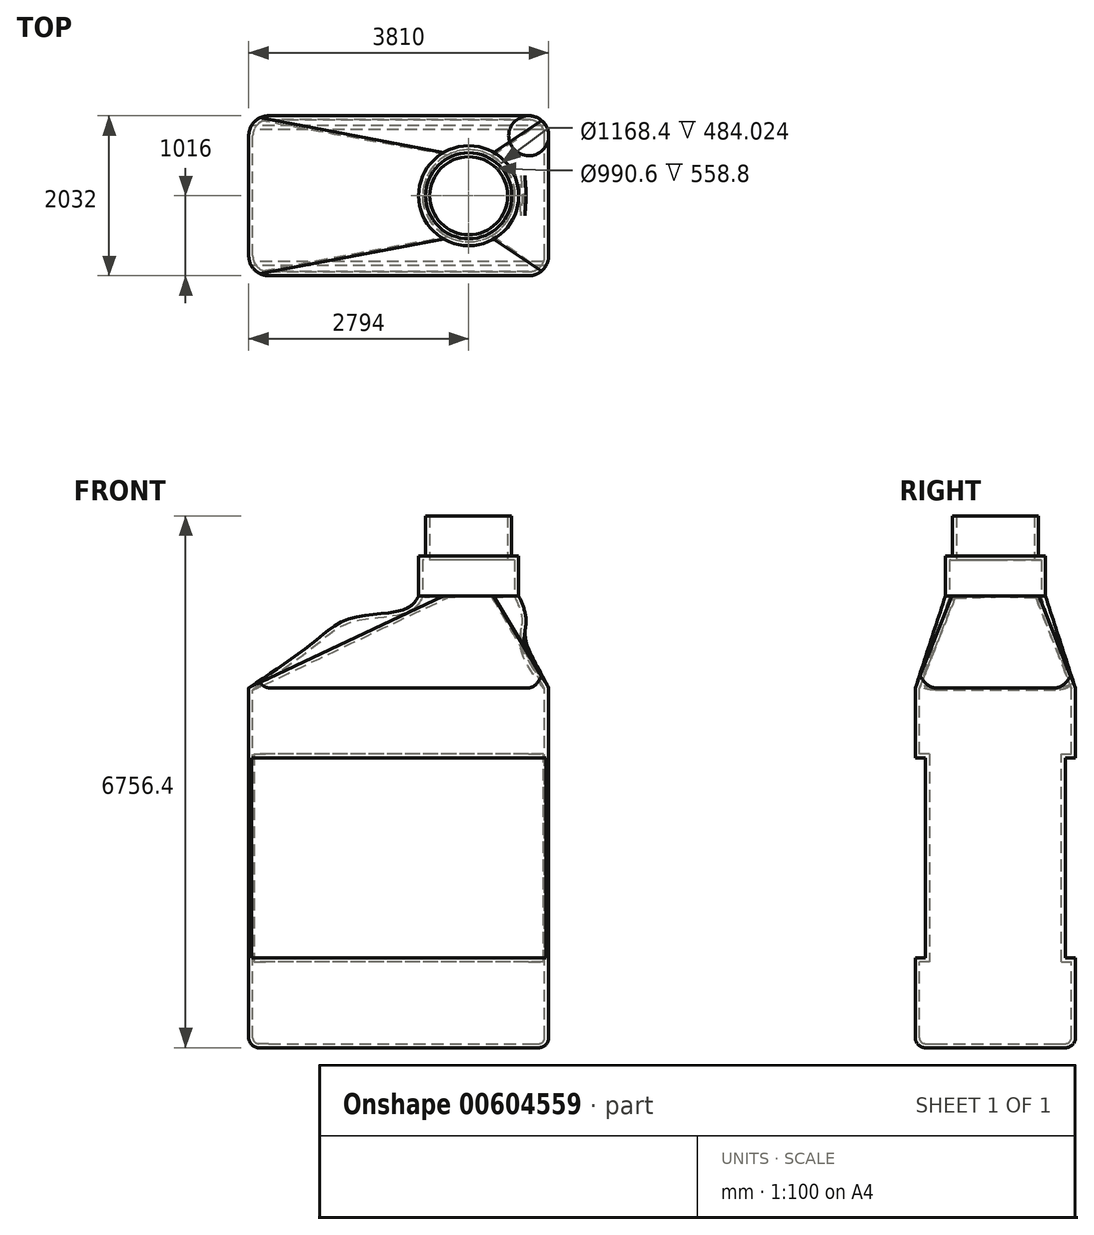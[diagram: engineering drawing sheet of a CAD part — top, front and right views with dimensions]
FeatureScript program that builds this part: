
annotation { "Feature Type Name" : "Feature", "Feature Type Description" : "" }
export const myFeature = defineFeature(function(context is Context, id is Id, definition is map)
    precondition{}
    {
        {
            var Q0;
            Q0=qCreatedBy(makeId("Top.planeOp"),FACE);
            var sketch = newSketch(context, id + "F0", { "sketchPlane" : qUnion([Q0])});
            skLineSegment(sketch, "E0.bottom", {"start": v(0, 0) * mm, "end": v(3810, 0) * mm});
            skLineSegment(sketch, "E0.top", {"start": v(0, 2032) * mm, "end": v(3810, 2032) * mm});
            skLineSegment(sketch, "E0.left", {"start": v(0, 0) * mm, "end": v(0, 2032) * mm});
            skLineSegment(sketch, "E0.right", {"start": v(3810, 0) * mm, "end": v(3810, 2032) * mm});
            skSolve(sketch);
        }
        {
            var Q0;
            Q0 = qSketchRegion(id + "F0", true);
            var Q1;
            Q1=makeQuery(id+"F0.imprint","IMPRINT",FACE,{"disambiguationData":[TD([[makeQuery(id+"F0.imprint","IMPRINT",EDGE,{"derivedFrom":sQuery(id+"F0.wireOp",EDGE,"E0.bottom")}),1.0]])]});
            extrude(context, id + "F1", {"entities" : qUnion([Q0, Q1]), "endBound" : BoundingType.SYMMETRIC, "depth" : 4572 * mm, "offsetDistance" : 25.4 * mm});
        }
        {
            var Q0;
            Q0=makeQuery(id+"F1.opExtrude","CAP_FACE",FACE,{"disambiguationData":[OSD([sQuery(id+"F0.wireOp",EDGE,"E0.bottom"),sQuery(id+"F0.wireOp",EDGE,"E0.top"),sQuery(id+"F0.wireOp",EDGE,"E0.left"),sQuery(id+"F0.wireOp",EDGE,"E0.right")])],"isStart":false});
            cPlane(context, id + "F2", {"entities" : qUnion([Q0]), "cplaneType" : CPlaneType.OFFSET, "offset" : 1168.4 * mm, "width" : 152.4 * mm, "height" : 152.4 * mm});
        }
        {
            var Q0;
            Q0=qCreatedBy(id+"F2.planeOp",FACE);
            var sketch = newSketch(context, id + "F3", { "sketchPlane" : qUnion([Q0])});
            skCircle(sketch, "E1", {"center": v(2794, 1016) * mm, "radius": 635 * mm});
            skSolve(sketch);
        }
        {
            var Q0;
            Q0=makeQuery(id+"F3.imprint","IMPRINT",FACE,{"disambiguationData":[TD([[makeQuery(id+"F3.imprint","IMPRINT",EDGE,{"derivedFrom":sQuery(id+"F3.wireOp",EDGE,"E1")}),1.0]])]});
            var Q1;
            Q1=sQuery(id+"F3.wireOp",EDGE,"E1");
            extrude(context, id + "F4", {"entities" : qUnion([Q0]), "surfaceEntities" : qUnion([Q1]), "depth" : 508 * mm, "offsetDistance" : 25.4 * mm});
        }
        {
            var Q0;
            Q0=makeQuery(id+"F4.opExtrude","CAP_FACE",FACE,{"disambiguationData":[OSD([sQuery(id+"F3.wireOp",EDGE,"E1")])],"isStart":false});
            var sketch = newSketch(context, id + "F5", { "sketchPlane" : qUnion([Q0])});
            skCircle(sketch, "E2", {"center": v(2794, 1016) * mm, "radius": 546.1 * mm});
            skSolve(sketch);
        }
        {
            var Q0;
            Q0=makeQuery(id+"F5.imprint","IMPRINT",FACE,{"disambiguationData":[TD([[makeQuery(id+"F5.imprint","IMPRINT",EDGE,{"derivedFrom":sQuery(id+"F5.wireOp",EDGE,"E2")}),1.0]])]});
            extrude(context, id + "F6", {"entities" : qUnion([Q0]), "operationType" : NewBodyOperationType.ADD, "depth" : 508 * mm, "offsetDistance" : 25.4 * mm});
        }
        {
            var Q0;
            Q0=makeQuery(id+"F1.opExtrude","SWEPT_FACE",FACE,{"disambiguationData":[OSD([sQuery(id+"F0.wireOp",EDGE,"E0.bottom")])]});
            var Q1;
            Q1=makeQuery(id+"F1.opExtrude","SWEPT_FACE",FACE,{"disambiguationData":[OSD([sQuery(id+"F0.wireOp",EDGE,"E0.top")])]});
            cPlane(context, id + "F7", {"entities" : qUnion([Q0, Q1]), "cplaneType" : CPlaneType.MID_PLANE, "offset" : 25.4 * mm, "width" : 152.4 * mm, "height" : 152.4 * mm});
        }
        {
            var Q0;
            Q0=qCreatedBy(id+"F7.planeOp",FACE);
            var sketch = newSketch(context, id + "F8", { "sketchPlane" : qUnion([Q0])});
            skLineSegment(sketch, "E3.0", {"start": v(0, 2286) * mm, "end": v(3810, 2286) * mm, "construction": true});
            skLineSegment(sketch, "E4.1", {"start": v(2159, 3454.4) * mm, "end": v(3429, 3454.4) * mm, "construction": true});
            skFitSpline(sketch, "E5", {"points": [v(3810, 2286) * mm, v(3502.07, 2804.73) * mm, v(3521.76, 3148.6) * mm, v(3429, 3454.4) * mm], "startDerivative": vector(-1043.9, 1329.22) * mm, "endDerivative": vector(-461.76, 1029.77) * mm});
            skFitSpline(sketch, "E6", {"points": [v(0, 2286) * mm, v(826.85, 2867.04) * mm, v(1279.75, 3162.6) * mm, v(1997.53, 3289.6) * mm, v(2159, 3454.4) * mm], "startDerivative": vector(2814.6, 1867.49) * mm, "endDerivative": vector(680.46, 1210.27) * mm});
            skSolve(sketch);
        }
        {
            var Q1;
            Q1=makeQuery(id+"F1.opExtrude","CAP_FACE",FACE,{"disambiguationData":[OSD([sQuery(id+"F0.wireOp",EDGE,"E0.bottom"),sQuery(id+"F0.wireOp",EDGE,"E0.top"),sQuery(id+"F0.wireOp",EDGE,"E0.left"),sQuery(id+"F0.wireOp",EDGE,"E0.right")])],"isStart":false});
            var Q2;
            Q2=makeQuery(id+"F4.opExtrude","CAP_FACE",FACE,{"disambiguationData":[OSD([sQuery(id+"F3.wireOp",EDGE,"E1")])],"isStart":true});
            var Q3;
            Q3=sQuery(id+"F8.wireOp",EDGE,"E6");
            var Q4;
            Q4=sQuery(id+"F8.wireOp",EDGE,"E5");
            loft(context, id + "F9", {"operationType" : NewBodyOperationType.ADD, "addGuides" : true, "sheetProfilesArray" : [{ "sheetProfileEntities" : qUnion([Q1]) }, { "sheetProfileEntities" : qUnion([Q2]) }], "guidesArray" : [{ "guideEntities" : qUnion([Q3]), "guideDerivativeType" : LoftGuideDerivativeType.DEFAULT, "guideDerivativeMagnitude" : 1 }, { "guideEntities" : qUnion([Q4]), "guideDerivativeType" : LoftGuideDerivativeType.DEFAULT, "guideDerivativeMagnitude" : 1 }]});
        }
        {
            var Q0;
            Q0=makeQuery(id+"F1.opExtrude","SWEPT_FACE",FACE,{"disambiguationData":[OSD([sQuery(id+"F0.wireOp",EDGE,"E0.top")])]});
            var sketch = newSketch(context, id + "F10", { "sketchPlane" : qUnion([Q0])});
            skLineSegment(sketch, "E7.bottom", {"start": v(-3810, 1397) * mm, "end": v(0, 1397) * mm});
            skLineSegment(sketch, "E7.top", {"start": v(-3810, -1143) * mm, "end": v(0, -1143) * mm});
            skLineSegment(sketch, "E7.left", {"start": v(-3810, 1397) * mm, "end": v(-3810, -1143) * mm});
            skLineSegment(sketch, "E7.right", {"start": v(0, 1397) * mm, "end": v(0, -1143) * mm});
            skSolve(sketch);
        }
        {
            var Q0;
            Q0=makeQuery(id+"F10.imprint","IMPRINT",FACE,{"disambiguationData":[TD([[makeQuery(id+"F10.imprint","IMPRINT",EDGE,{"derivedFrom":sQuery(id+"F10.wireOp",EDGE,"E7.bottom")}),-1.0]])]});
            extrude(context, id + "F11", {"entities" : qUnion([Q0]), "operationType" : NewBodyOperationType.REMOVE, "oppositeDirection" : true, "depth" : 127 * mm, "offsetDistance" : 25.4 * mm});
        }
        {
            var Q0;
            Q0=makeQuery(id+"F1.opExtrude","SWEPT_FACE",FACE,{"disambiguationData":[OSD([sQuery(id+"F0.wireOp",EDGE,"E0.bottom")])]});
            var sketch = newSketch(context, id + "F12", { "sketchPlane" : qUnion([Q0])});
            skLineSegment(sketch, "E8.0", {"start": v(3810, 1397) * mm, "end": v(0, 1397) * mm});
            skLineSegment(sketch, "E9.0", {"start": v(3810, 1397) * mm, "end": v(3810, -1143) * mm});
            skLineSegment(sketch, "E10.0", {"start": v(3810, -1143) * mm, "end": v(0, -1143) * mm});
            skLineSegment(sketch, "E11.0", {"start": v(0, 1397) * mm, "end": v(0, -1143) * mm});
            skSolve(sketch);
        }
        {
            var Q0;
            Q0=makeQuery(id+"F12.imprint","IMPRINT",FACE,{"disambiguationData":[TD([[makeQuery(id+"F12.imprint","IMPRINT",EDGE,{"derivedFrom":sQuery(id+"F12.wireOp",EDGE,"E8.0")}),1.0]])]});
            extrude(context, id + "F13", {"entities" : qUnion([Q0]), "operationType" : NewBodyOperationType.REMOVE, "oppositeDirection" : true, "depth" : 127 * mm, "offsetDistance" : 25.4 * mm});
        }
        {
            var Q0;
            {var subQ3=sQuery(id+"F0.wireOp",EDGE,"E0.left");var subQ4=sQuery(id+"F0.wireOp",EDGE,"E0.bottom");Q0=makeQuery(id+"F13.boolean.opBoolean","SPLIT",EDGE,{"disambiguationData":[TD([makeQuery(id+"F13.opExtrude","SWEPT_FACE",FACE,{"disambiguationData":[OSD([sQuery(id+"F12.wireOp",EDGE,"E8.0")])]})])],"derivedFrom":makeQuery(id+"F1.opExtrude","SWEPT_EDGE",EDGE,{"disambiguationData":[OSD([subQ4,subQ3])]})});}
            var Q1;
            {var subQ0=sQuery(id+"F0.wireOp",EDGE,"E0.bottom");var subQ1=sQuery(id+"F0.wireOp",EDGE,"E0.left");Q1=makeQuery(id+"F13.boolean.opBoolean","SPLIT",EDGE,{"disambiguationData":[TD([makeQuery(id+"F13.opExtrude","SWEPT_FACE",FACE,{"disambiguationData":[OSD([sQuery(id+"F12.wireOp",EDGE,"E10.0")])]})])],"derivedFrom":makeQuery(id+"F1.opExtrude","SWEPT_EDGE",EDGE,{"disambiguationData":[OSD([subQ0,subQ1])]})});}
            var Q2;
            {var subQ0=sQuery(id+"F0.wireOp",EDGE,"E0.left");var subQ1=sQuery(id+"F0.wireOp",EDGE,"E0.top");Q2=makeQuery(id+"F11.boolean.opBoolean","SPLIT",EDGE,{"disambiguationData":[TD([makeQuery(id+"F11.opExtrude","SWEPT_FACE",FACE,{"disambiguationData":[OSD([sQuery(id+"F10.wireOp",EDGE,"E7.top")])]})])],"derivedFrom":makeQuery(id+"F1.opExtrude","SWEPT_EDGE",EDGE,{"disambiguationData":[OSD([subQ1,subQ0])]})});}
            var Q3;
            {var subQ2=sQuery(id+"F0.wireOp",EDGE,"E0.left");var subQ3=sQuery(id+"F0.wireOp",EDGE,"E0.top");Q3=makeQuery(id+"F11.boolean.opBoolean","SPLIT",EDGE,{"disambiguationData":[TD([makeQuery(id+"F11.opExtrude","SWEPT_FACE",FACE,{"disambiguationData":[OSD([sQuery(id+"F10.wireOp",EDGE,"E7.bottom")])]})])],"derivedFrom":makeQuery(id+"F1.opExtrude","SWEPT_EDGE",EDGE,{"disambiguationData":[OSD([subQ3,subQ2])]})});}
            var Q4;
            {var subQ0=sQuery(id+"F0.wireOp",EDGE,"E0.bottom");var subQ1=sQuery(id+"F0.wireOp",EDGE,"E0.right");Q4=makeQuery(id+"F13.boolean.opBoolean","SPLIT",EDGE,{"disambiguationData":[TD([makeQuery(id+"F13.opExtrude","SWEPT_FACE",FACE,{"disambiguationData":[OSD([sQuery(id+"F12.wireOp",EDGE,"E10.0")])]})])],"derivedFrom":makeQuery(id+"F1.opExtrude","SWEPT_EDGE",EDGE,{"disambiguationData":[OSD([subQ0,subQ1])]})});}
            var Q5;
            {var subQ1=sQuery(id+"F0.wireOp",EDGE,"E0.right");var subQ3=sQuery(id+"F0.wireOp",EDGE,"E0.bottom");Q5=makeQuery(id+"F13.boolean.opBoolean","SPLIT",EDGE,{"disambiguationData":[TD([makeQuery(id+"F13.opExtrude","SWEPT_FACE",FACE,{"disambiguationData":[OSD([sQuery(id+"F12.wireOp",EDGE,"E8.0")])]})])],"derivedFrom":makeQuery(id+"F1.opExtrude","SWEPT_EDGE",EDGE,{"disambiguationData":[OSD([subQ3,subQ1])]})});}
            var Q6;
            {var subQ2=sQuery(id+"F0.wireOp",EDGE,"E0.right");var subQ4=sQuery(id+"F0.wireOp",EDGE,"E0.top");Q6=makeQuery(id+"F11.boolean.opBoolean","SPLIT",EDGE,{"disambiguationData":[TD([makeQuery(id+"F11.opExtrude","SWEPT_FACE",FACE,{"disambiguationData":[OSD([sQuery(id+"F10.wireOp",EDGE,"E7.bottom")])]})])],"derivedFrom":makeQuery(id+"F1.opExtrude","SWEPT_EDGE",EDGE,{"disambiguationData":[OSD([subQ4,subQ2])]})});}
            var Q7;
            {var subQ0=sQuery(id+"F0.wireOp",EDGE,"E0.right");var subQ1=sQuery(id+"F0.wireOp",EDGE,"E0.top");Q7=makeQuery(id+"F11.boolean.opBoolean","SPLIT",EDGE,{"disambiguationData":[TD([makeQuery(id+"F11.opExtrude","SWEPT_FACE",FACE,{"disambiguationData":[OSD([sQuery(id+"F10.wireOp",EDGE,"E7.top")])]})])],"derivedFrom":makeQuery(id+"F1.opExtrude","SWEPT_EDGE",EDGE,{"disambiguationData":[OSD([subQ1,subQ0])]})});}
            fillet(context, id + "F14", {"entities" : qUnion([Q0, Q1, Q2, Q3, Q4, Q5, Q6, Q7]), "radius" : 254 * mm, "tangentPropagation" : true, "allowEdgeOverflow" : false});
        }
        {
            var Q0;
            Q0=makeQuery(id+"F1.opExtrude","CAP_EDGE",EDGE,{"disambiguationData":[OSD([sQuery(id+"F0.wireOp",EDGE,"E0.bottom")])],"isStart":true});
            var Q1;
            {var subQ0=sQuery(id+"F0.wireOp",EDGE,"E0.right");var subQ1=sQuery(id+"F0.wireOp",EDGE,"E0.left");var subQ2=sQuery(id+"F0.wireOp",EDGE,"E0.top");var subQ3=sQuery(id+"F0.wireOp",EDGE,"E0.bottom");Q1=makeQuery(id+"F14.opFillet","BLEND_EDGE",EDGE,{"blendedFrom":[makeQuery(id+"F13.boolean.opBoolean","SPLIT",EDGE,{"disambiguationData":[TD([makeQuery(id+"F13.opExtrude","SWEPT_FACE",FACE,{"disambiguationData":[OSD([sQuery(id+"F12.wireOp",EDGE,"E8.0")])]})])],"derivedFrom":makeQuery(id+"F1.opExtrude","SWEPT_EDGE",EDGE,{"disambiguationData":[OSD([subQ3,subQ1])]})}),makeQuery(id+"F1.opExtrude","CAP_FACE",FACE,{"disambiguationData":[OSD([subQ3,subQ2,subQ1,subQ0])],"isStart":true})],"blendedInto":[makeQuery(id+"F1.opExtrude","CAP_FACE",FACE,{"disambiguationData":[OSD([subQ3,subQ2,subQ1,subQ0])],"isStart":true})]});}
            var Q2;
            Q2=makeQuery(id+"F1.opExtrude","CAP_EDGE",EDGE,{"disambiguationData":[OSD([sQuery(id+"F0.wireOp",EDGE,"E0.left")])],"isStart":true});
            var Q3;
            Q3=makeQuery(id+"F1.opExtrude","CAP_EDGE",EDGE,{"disambiguationData":[OSD([sQuery(id+"F0.wireOp",EDGE,"E0.top")])],"isStart":true});
            var Q4;
            {var subQ0=sQuery(id+"F0.wireOp",EDGE,"E0.right");var subQ1=sQuery(id+"F0.wireOp",EDGE,"E0.left");var subQ2=sQuery(id+"F0.wireOp",EDGE,"E0.top");Q4=makeQuery(id+"F14.opFillet","BLEND_EDGE",EDGE,{"blendedFrom":[makeQuery(id+"F11.boolean.opBoolean","SPLIT",EDGE,{"disambiguationData":[TD([makeQuery(id+"F11.opExtrude","SWEPT_FACE",FACE,{"disambiguationData":[OSD([sQuery(id+"F10.wireOp",EDGE,"E7.bottom")])]})])],"derivedFrom":makeQuery(id+"F1.opExtrude","SWEPT_EDGE",EDGE,{"disambiguationData":[OSD([subQ2,subQ1])]})}),makeQuery(id+"F1.opExtrude","CAP_FACE",FACE,{"disambiguationData":[OSD([sQuery(id+"F0.wireOp",EDGE,"E0.bottom"),subQ2,subQ1,subQ0])],"isStart":true})],"blendedInto":[makeQuery(id+"F1.opExtrude","CAP_FACE",FACE,{"disambiguationData":[OSD([sQuery(id+"F0.wireOp",EDGE,"E0.bottom"),subQ2,subQ1,subQ0])],"isStart":true})]});}
            var Q5;
            Q5=makeQuery(id+"F1.opExtrude","CAP_EDGE",EDGE,{"disambiguationData":[OSD([sQuery(id+"F0.wireOp",EDGE,"E0.right")])],"isStart":true});
            var Q6;
            {var subQ0=sQuery(id+"F0.wireOp",EDGE,"E0.right");var subQ1=sQuery(id+"F0.wireOp",EDGE,"E0.left");var subQ2=sQuery(id+"F0.wireOp",EDGE,"E0.bottom");Q6=makeQuery(id+"F14.opFillet","BLEND_EDGE",EDGE,{"blendedFrom":[makeQuery(id+"F13.boolean.opBoolean","SPLIT",EDGE,{"disambiguationData":[TD([makeQuery(id+"F13.opExtrude","SWEPT_FACE",FACE,{"disambiguationData":[OSD([sQuery(id+"F12.wireOp",EDGE,"E8.0")])]})])],"derivedFrom":makeQuery(id+"F1.opExtrude","SWEPT_EDGE",EDGE,{"disambiguationData":[OSD([subQ2,subQ0])]})}),makeQuery(id+"F1.opExtrude","CAP_FACE",FACE,{"disambiguationData":[OSD([subQ2,sQuery(id+"F0.wireOp",EDGE,"E0.top"),subQ1,subQ0])],"isStart":true})],"blendedInto":[makeQuery(id+"F1.opExtrude","CAP_FACE",FACE,{"disambiguationData":[OSD([subQ2,sQuery(id+"F0.wireOp",EDGE,"E0.top"),subQ1,subQ0])],"isStart":true})]});}
            var Q7;
            {var subQ0=sQuery(id+"F0.wireOp",EDGE,"E0.right");var subQ1=sQuery(id+"F0.wireOp",EDGE,"E0.left");var subQ2=sQuery(id+"F0.wireOp",EDGE,"E0.top");var subQ3=sQuery(id+"F0.wireOp",EDGE,"E0.bottom");Q7=makeQuery(id+"F14.opFillet","BLEND_EDGE",EDGE,{"blendedFrom":[makeQuery(id+"F11.boolean.opBoolean","SPLIT",EDGE,{"disambiguationData":[TD([makeQuery(id+"F11.opExtrude","SWEPT_FACE",FACE,{"disambiguationData":[OSD([sQuery(id+"F10.wireOp",EDGE,"E7.bottom")])]})])],"derivedFrom":makeQuery(id+"F1.opExtrude","SWEPT_EDGE",EDGE,{"disambiguationData":[OSD([subQ2,subQ0])]})}),makeQuery(id+"F1.opExtrude","CAP_FACE",FACE,{"disambiguationData":[OSD([subQ3,subQ2,subQ1,subQ0])],"isStart":true})],"blendedInto":[makeQuery(id+"F1.opExtrude","CAP_FACE",FACE,{"disambiguationData":[OSD([subQ3,subQ2,subQ1,subQ0])],"isStart":true})]});}
            fillet(context, id + "F15", {"entities" : qUnion([Q0, Q1, Q2, Q3, Q4, Q5, Q6, Q7]), "radius" : 127 * mm, "tangentPropagation" : true, "allowEdgeOverflow" : false});
        }
        {
            var Q0;
            Q0=makeQuery(id+"F6.opExtrude","CAP_FACE",FACE,{"disambiguationData":[OSD([sQuery(id+"F5.wireOp",EDGE,"E2")])],"isStart":false});
            shell(context, id + "F16", {"entities" : qUnion([Q0]), "thickness" : 50.8 * mm});
        }
    });
